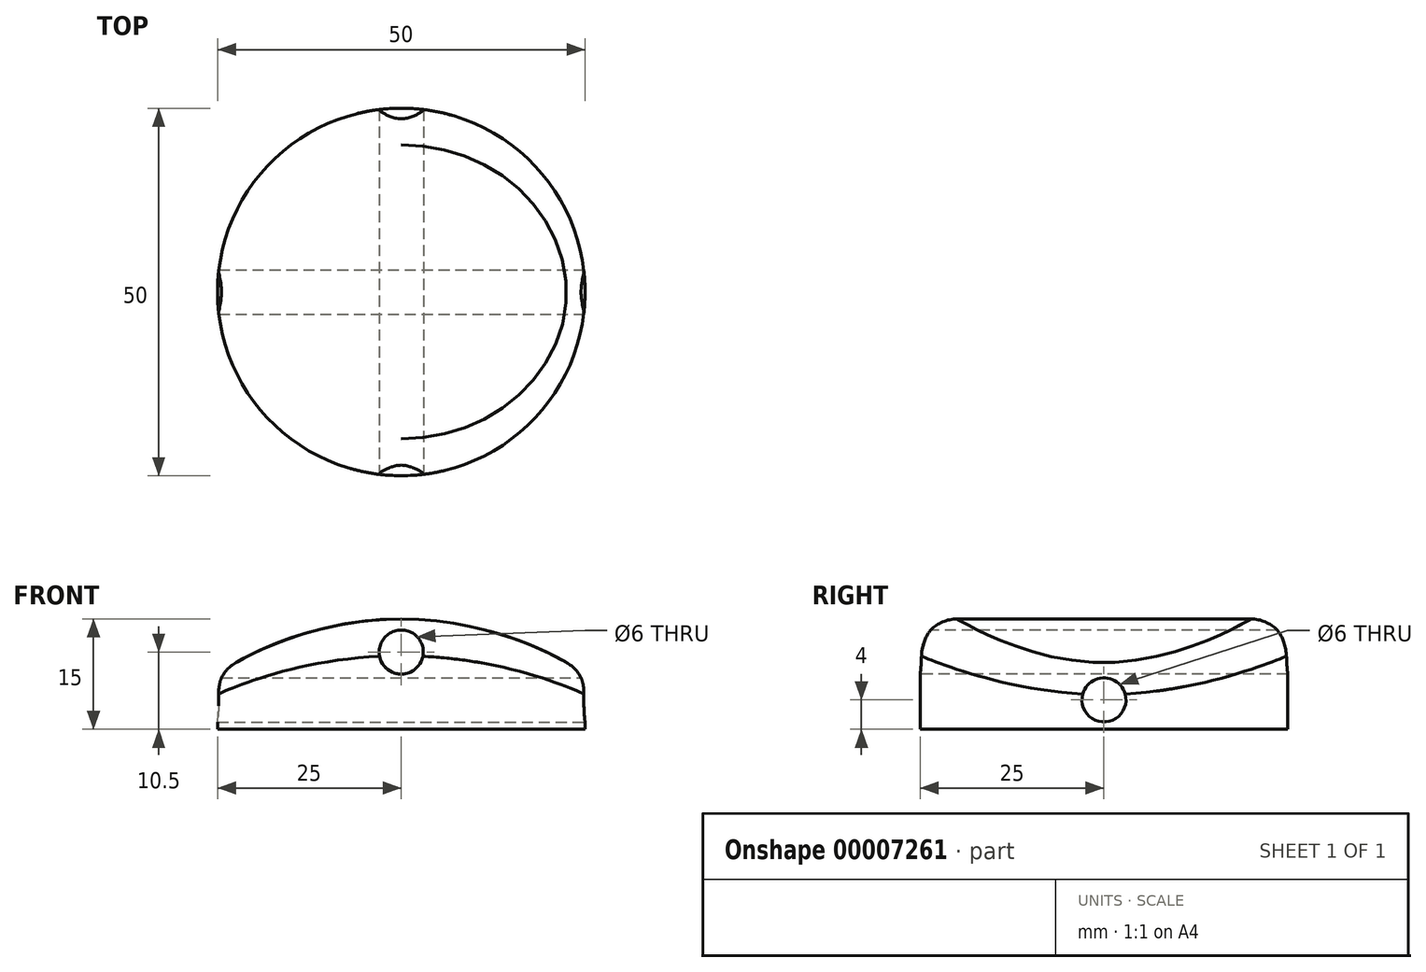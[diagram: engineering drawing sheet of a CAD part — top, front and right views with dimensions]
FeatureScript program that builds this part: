
annotation { "Feature Type Name" : "Feature", "Feature Type Description" : "" }
export const myFeature = defineFeature(function(context is Context, id is Id, definition is map)
    precondition{}
    {
        {
            var Q0;
            Q0=qCreatedBy(makeId("Top.planeOp"),FACE);
            var sketch = newSketch(context, id + "F0", { "sketchPlane" : qUnion([Q0])});
            skCircle(sketch, "E0", {"center": v(0, 0) * mm, "radius": 25 * mm});
            skSolve(sketch);
        }
        {
            var Q0;
            Q0=makeQuery(id+"F0.imprint","IMPRINT",FACE,{"disambiguationData":[TD([[makeQuery(id+"F0.imprint","IMPRINT",EDGE,{"derivedFrom":sQuery(id+"F0.wireOp",EDGE,"E0")}),1.0]])]});
            extrude(context, id + "F1", {"entities" : qUnion([Q0]), "depth" : 15 * mm});
        }
        {
            var Q0;
            Q0=qCreatedBy(makeId("Front.planeOp"),FACE);
            var sketch = newSketch(context, id + "F2", { "sketchPlane" : qUnion([Q0])});
            skLineSegment(sketch, "E1.0", {"start": v(-25, 15) * mm, "end": v(25, 15) * mm});
            skLineSegment(sketch, "E2.0.0", {"start": v(25, 0) * mm, "end": v(-25, 0) * mm});
            skLineSegment(sketch, "E3", {"start": v(-25, 15) * mm, "end": v(-25, 0) * mm});
            skLineSegment(sketch, "E4", {"start": v(25, 0) * mm, "end": v(25, 15) * mm});
            skFitSpline(sketch, "E5", {"points": [v(-25, 7.5) * mm, v(-15.44, 12.28) * mm, v(0, 15) * mm], "startDerivative": vector(18.03, 12.35) * mm, "endDerivative": vector(32.01, 0) * mm});
            skFitSpline(sketch, "E6.0.MirrorCS", {"points": [v(25, 7.5) * mm, v(15.44, 12.28) * mm, v(0, 15) * mm], "startDerivative": vector(-18.03, 12.35) * mm, "endDerivative": vector(-32.01, 0) * mm});
            skSolve(sketch);
        }
        {
            var Q0;
            {var subQ0=sQuery(id+"F2.wireOp",EDGE,"E5");Q0=makeQuery(id+"F2.imprint","IMPRINT",FACE,{"disambiguationData":[TD([[makeQuery(id+"F2.imprint","IMPRINT",EDGE,{"derivedFrom":subQ0}),1.0]])]});}
            var Q1;
            {var subQ0=sQuery(id+"F2.wireOp",EDGE,"E6.0.MirrorCS");Q1=makeQuery(id+"F2.imprint","IMPRINT",FACE,{"disambiguationData":[TD([[makeQuery(id+"F2.imprint","IMPRINT",EDGE,{"derivedFrom":subQ0}),-1.0]])]});}
            extrude(context, id + "F3", {"entities" : qUnion([Q0, Q1]), "operationType" : NewBodyOperationType.REMOVE, "endBound" : BoundingType.SYMMETRIC, "oppositeDirection" : true, "depth" : 50 * mm});
        }
        {
            var Q0;
            Q0=qCreatedBy(makeId("Front.planeOp"),FACE);
            var sketch = newSketch(context, id + "F4", { "sketchPlane" : qUnion([Q0])});
            skLineSegment(sketch, "E7.0", {"start": v(-25, 0) * mm, "end": v(25, 0) * mm});
            skLineSegment(sketch, "E8", {"start": v(0, 0) * mm, "end": v(0, 10.5) * mm, "construction": true});
            skCircle(sketch, "E9", {"center": v(0, 10.5) * mm, "radius": 3 * mm});
            skSolve(sketch);
        }
        {
            var Q0;
            Q0=makeQuery(id+"F4.imprint","IMPRINT",FACE,{"disambiguationData":[TD([[makeQuery(id+"F4.imprint","IMPRINT",EDGE,{"derivedFrom":sQuery(id+"F4.wireOp",EDGE,"E9")}),1.0]])]});
            extrude(context, id + "F5", {"entities" : qUnion([Q0]), "operationType" : NewBodyOperationType.REMOVE, "endBound" : BoundingType.SYMMETRIC, "oppositeDirection" : true, "depth" : 50 * mm});
        }
        {
            var Q0;
            Q0=qCreatedBy(makeId("Right.planeOp"),FACE);
            var sketch = newSketch(context, id + "F6", { "sketchPlane" : qUnion([Q0])});
            skLineSegment(sketch, "E10", {"start": v(0, 0) * mm, "end": v(0, 4) * mm, "construction": true});
            skCircle(sketch, "E11", {"center": v(0, 4) * mm, "radius": 3 * mm});
            skSolve(sketch);
        }
        {
            var Q0;
            Q0=makeQuery(id+"F6.imprint","IMPRINT",FACE,{"disambiguationData":[TD([[makeQuery(id+"F6.imprint","IMPRINT",EDGE,{"derivedFrom":sQuery(id+"F6.wireOp",EDGE,"E11")}),1.0]])]});
            extrude(context, id + "F7", {"entities" : qUnion([Q0]), "operationType" : NewBodyOperationType.REMOVE, "endBound" : BoundingType.SYMMETRIC, "oppositeDirection" : true, "depth" : 50 * mm});
        }
        {
            var Q0;
            Q0=makeQuery(id+"F3.boolean.opBoolean","INTERSECT",EDGE,{"derivedFrom":[makeQuery(id+"F1.opExtrude","SWEPT_FACE",FACE,{"disambiguationData":[OSD([sQuery(id+"F0.wireOp",EDGE,"E0")])]}),makeQuery(id+"F3.opExtrude","SWEPT_FACE",FACE,{"disambiguationData":[OSD([sQuery(id+"F2.wireOp",EDGE,"E5")])]})]});
            var Q1;
            Q1=makeQuery(id+"F3.boolean.opBoolean","INTERSECT",EDGE,{"derivedFrom":[makeQuery(id+"F1.opExtrude","SWEPT_FACE",FACE,{"disambiguationData":[OSD([sQuery(id+"F0.wireOp",EDGE,"E0")])]}),makeQuery(id+"F3.opExtrude","SWEPT_FACE",FACE,{"disambiguationData":[OSD([sQuery(id+"F2.wireOp",EDGE,"E6.0.MirrorCS")])]})]});
            fillet(context, id + "F8", {"entities" : qUnion([Q0, Q1]), "radius" : 5 * mm, "tangentPropagation" : true, "allowEdgeOverflow" : false});
        }
    });
